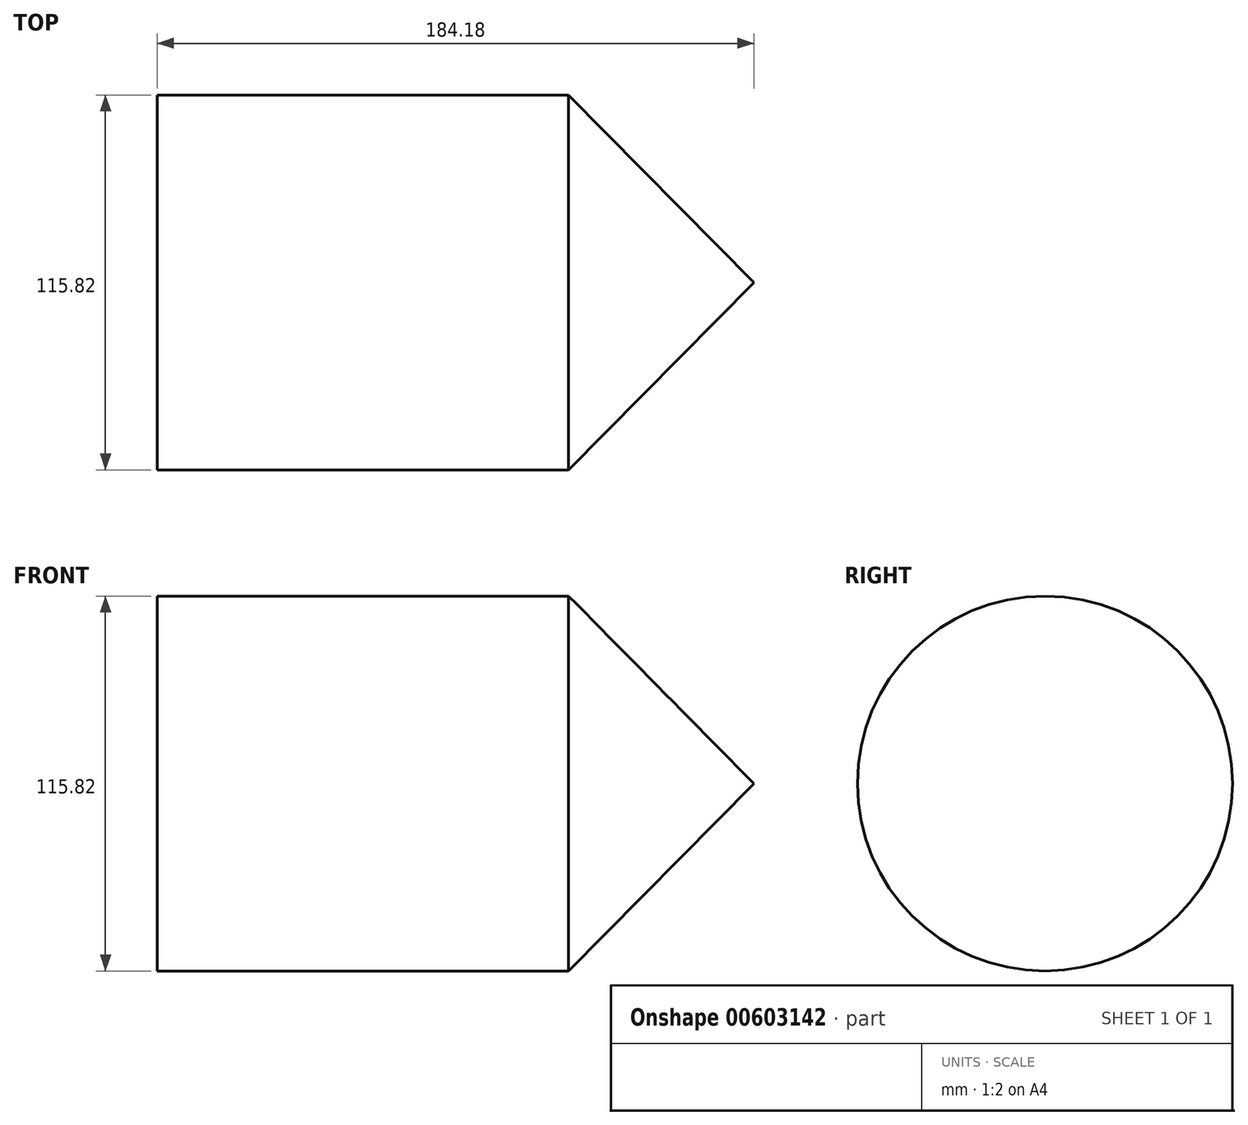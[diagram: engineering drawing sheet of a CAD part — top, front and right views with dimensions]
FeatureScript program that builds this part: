
annotation { "Feature Type Name" : "Feature", "Feature Type Description" : "" }
export const myFeature = defineFeature(function(context is Context, id is Id, definition is map)
    precondition{}
    {
        {
            var Q0;
            Q0=qCreatedBy(makeId("Front.planeOp"),FACE);
            var sketch = newSketch(context, id + "F0", { "sketchPlane" : qUnion([Q0])});
            skLineSegment(sketch, "E0", {"start": v(0, -57.91) * mm, "end": v(57.18, -57.91) * mm});
            skLineSegment(sketch, "E1", {"start": v(57.18, -57.91) * mm, "end": v(0, 0) * mm});
            skLineSegment(sketch, "E2", {"start": v(0, 0) * mm, "end": v(0, -57.91) * mm});
            skSolve(sketch);
        }
        {
            var Q0;
            Q0 = qSketchRegion(id + "F0", true);
            var Q1;
            Q1=sQuery(id+"F0.wireOp",EDGE,"E0");
            revolve(context, id + "F1", {"entities" : qUnion([Q0]), "axis" : qUnion([Q1]), "revolveType" : RevolveType.FULL});
        }
        {
            var Q0;
            Q0=makeQuery(id+"F1.opRevolve","SWEPT_FACE",FACE,{"disambiguationData":[OSD([sQuery(id+"F0.wireOp",EDGE,"E2")])]});
            extrude(context, id + "F2", {"entities" : qUnion([Q0]), "operationType" : NewBodyOperationType.ADD, "depth" : 127 * mm, "offsetDistance" : 25.4 * mm});
        }
    });
